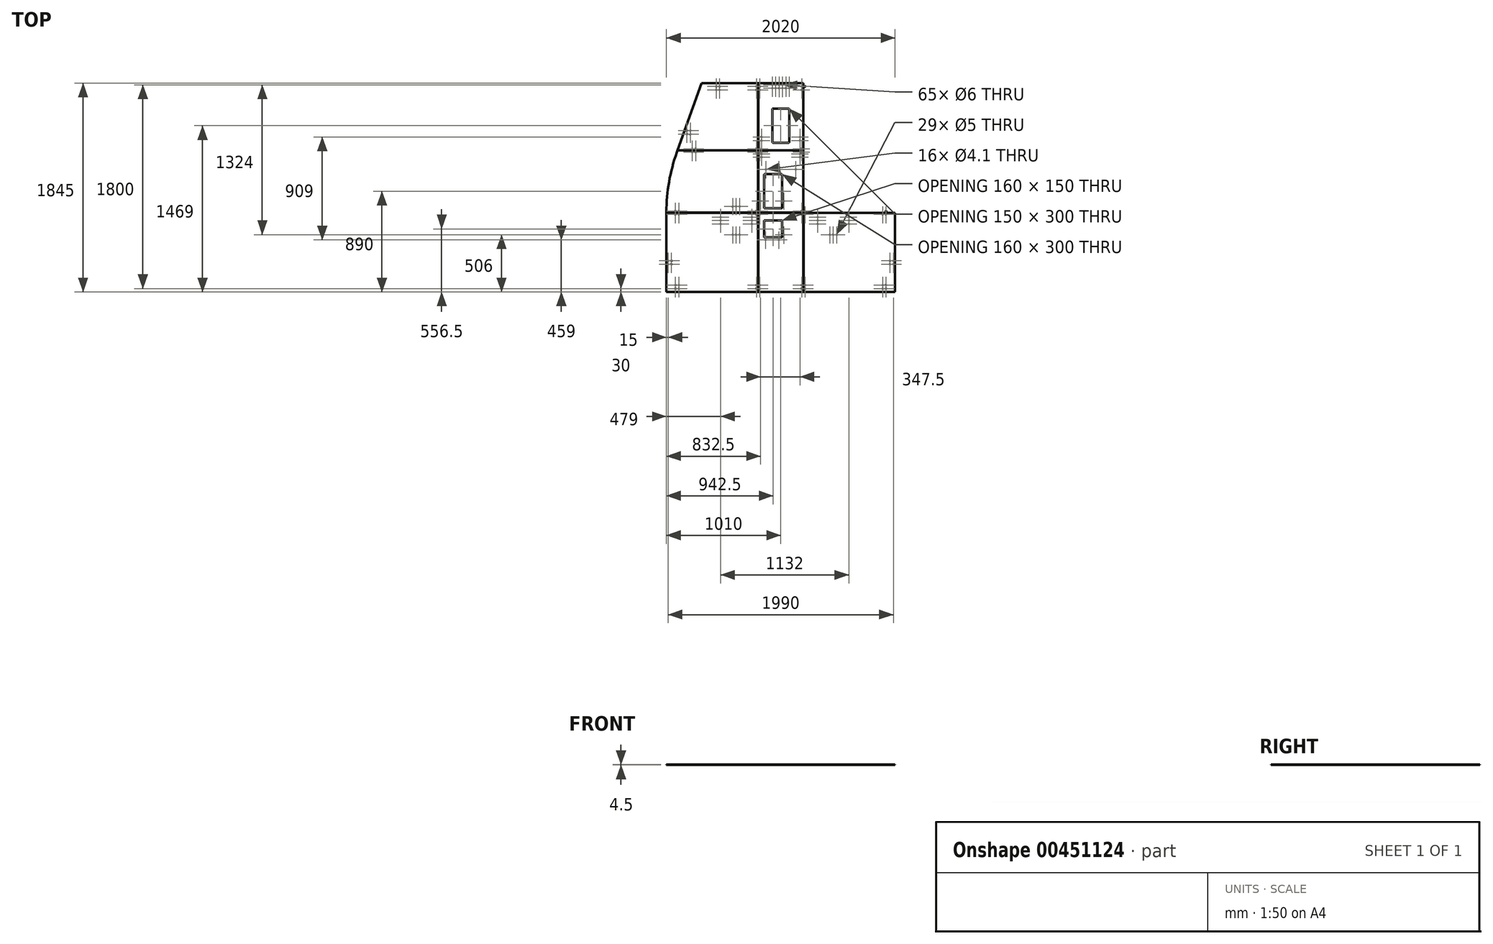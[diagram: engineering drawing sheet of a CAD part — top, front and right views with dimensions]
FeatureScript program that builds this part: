
annotation { "Feature Type Name" : "Feature", "Feature Type Description" : "" }
export const myFeature = defineFeature(function(context is Context, id is Id, definition is map)
    precondition{}
    {
        {
            var Q0;
            Q0=qCreatedBy(makeId("Top.planeOp"),FACE);
            var sketch = newSketch(context, id + "F0", { "sketchPlane" : qUnion([Q0])});
            skLineSegment(sketch, "E0.bottom", {"start": v(200, -350) * mm, "end": v(-200, -350) * mm});
            skLineSegment(sketch, "E0.top", {"start": v(200, 350) * mm, "end": v(-200, 350) * mm});
            skLineSegment(sketch, "E0.left", {"start": v(200, -350) * mm, "end": v(200, 350) * mm});
            skLineSegment(sketch, "E0.right", {"start": v(-200, -350) * mm, "end": v(-200, 350) * mm});
            skPoint(sketch, "E0.middle", {"position": v(0, 0) * mm});
            skCircle(sketch, "E1", {"center": v(185, 335) * mm, "radius": 3 * mm});
            skCircle(sketch, "E2", {"center": v(-185, 335) * mm, "radius": 3 * mm});
            skCircle(sketch, "E3", {"center": v(185, -320) * mm, "radius": 3 * mm});
            skCircle(sketch, "E4", {"center": v(-185, -320) * mm, "radius": 3 * mm});
            skLineSegment(sketch, "E5.bottom", {"start": v(12.5, 131.5) * mm, "end": v(-147.5, 131.5) * mm});
            skLineSegment(sketch, "E5.top", {"start": v(12.5, 281.5) * mm, "end": v(-147.5, 281.5) * mm});
            skLineSegment(sketch, "E5.left", {"start": v(12.5, 131.5) * mm, "end": v(12.5, 281.5) * mm});
            skLineSegment(sketch, "E5.right", {"start": v(-147.5, 131.5) * mm, "end": v(-147.5, 281.5) * mm});
            skPoint(sketch, "E5.middle", {"position": v(-67.5, 206.5) * mm});
            skCircle(sketch, "E6", {"center": v(-134.5, 109) * mm, "radius": 2.05 * mm});
            skCircle(sketch, "E7", {"center": v(-17.5, 109) * mm, "radius": 2.05 * mm});
            skCircle(sketch, "E8", {"center": v(27.5, 154) * mm, "radius": 2.05 * mm});
            skCircle(sketch, "E9", {"center": v(-185, -290) * mm, "radius": 3 * mm});
            skCircle(sketch, "E10", {"center": v(185, -290) * mm, "radius": 3 * mm});
            skSolve(sketch);
        }
        {
            var Q0;
            Q0=qSketchRegion(id+"F0",true);
            extrude(context, id + "F1", {"entities" : qUnion([Q0]), "depth" : 4.5 * mm, "offsetDistance" : 25 * mm});
        }
        {
            var Q0;
            Q0=qCreatedBy(makeId("Top.planeOp"),FACE);
            var sketch = newSketch(context, id + "F2", { "sketchPlane" : qUnion([Q0])});
            skLineSegment(sketch, "E11.top", {"start": v(-200, 900) * mm, "end": v(-912, 900) * mm});
            skLineSegment(sketch, "E11.left", {"start": v(-200, 350) * mm, "end": v(-200, 900) * mm});
            skPoint(sketch, "E11.middle", {"position": v(-556, 625) * mm});
            skLineSegment(sketch, "E12", {"start": v(-200, 350) * mm, "end": v(-1010, 350) * mm});
            skCircle(sketch, "E13", {"center": v(-215, 885) * mm, "radius": 3 * mm});
            skCircle(sketch, "E14", {"center": v(-215, 365) * mm, "radius": 3 * mm});
            skCircle(sketch, "E15", {"center": v(-930, 365) * mm, "radius": 3 * mm});
            skCircle(sketch, "E16", {"center": v(-782, 885) * mm, "radius": 3 * mm});
            skLineSegment(sketch, "E17.left", {"start": v(-200, 900) * mm, "end": v(-200, 1495) * mm});
            skPoint(sketch, "E17.middle", {"position": v(-556, 1197.5) * mm});
            skLineSegment(sketch, "E18", {"start": v(-200, 1495) * mm, "end": v(-700, 1495) * mm});
            skLineSegment(sketch, "E19", {"start": v(-912, 900) * mm, "end": v(-700, 1495) * mm});
            skCircle(sketch, "E20", {"center": v(-215, 1465) * mm, "radius": 3 * mm});
            skCircle(sketch, "E21", {"center": v(-215, 915) * mm, "radius": 3 * mm});
            skCircle(sketch, "E22", {"center": v(-782, 915) * mm, "radius": 3 * mm});
            skCircle(sketch, "E23", {"center": v(-570, 1465) * mm, "radius": 3 * mm});
            skLineSegment(sketch, "E24", {"start": v(0, 1490.85) * mm, "end": v(0, 501.43) * mm, "construction": true});
            skCircle(sketch, "E25.MirrorC", {"center": v(215, 1465) * mm, "radius": 3 * mm});
            skCircle(sketch, "E26.MirrorC", {"center": v(930, 365) * mm, "radius": 3 * mm});
            skCircle(sketch, "E27.MirrorC", {"center": v(782, 885) * mm, "radius": 3 * mm});
            skCircle(sketch, "E28.MirrorC", {"center": v(782, 915) * mm, "radius": 3 * mm});
            skCircle(sketch, "E29.MirrorC", {"center": v(570, 1465) * mm, "radius": 3 * mm});
            skCircle(sketch, "E30.MirrorC", {"center": v(215, 885) * mm, "radius": 3 * mm});
            skCircle(sketch, "E31.MirrorC", {"center": v(215, 365) * mm, "radius": 3 * mm});
            skCircle(sketch, "E32.MirrorC", {"center": v(215, 915) * mm, "radius": 3 * mm});
            skLineSegment(sketch, "E33.MirrorCS", {"start": v(200, 1495) * mm, "end": v(700, 1495) * mm});
            skLineSegment(sketch, "E34.MirrorCS", {"start": v(1010, 350) * mm, "end": v(912, 900) * mm, "construction": true});
            skLineSegment(sketch, "E35.MirrorCS", {"start": v(200, 900) * mm, "end": v(912, 900) * mm});
            skPoint(sketch, "E36.MirrorP", {"position": v(556, 1197.5) * mm});
            skLineSegment(sketch, "E37.MirrorCS", {"start": v(200, 350) * mm, "end": v(200, 900) * mm});
            skPoint(sketch, "E38.MirrorP", {"position": v(556, 625) * mm});
            skLineSegment(sketch, "E39.MirrorCS", {"start": v(200, 350) * mm, "end": v(1010, 350) * mm});
            skLineSegment(sketch, "E40.MirrorCS", {"start": v(912, 900) * mm, "end": v(700, 1495) * mm});
            skLineSegment(sketch, "E41.MirrorCS", {"start": v(200, 900) * mm, "end": v(200, 1495) * mm});
            skCircle(sketch, "E42", {"center": v(-900, 365) * mm, "radius": 3 * mm});
            skCircle(sketch, "E43", {"center": v(-752, 885) * mm, "radius": 3 * mm});
            skCircle(sketch, "E44", {"center": v(-752, 915) * mm, "radius": 3 * mm});
            skCircle(sketch, "E45", {"center": v(-570, 1435) * mm, "radius": 3 * mm});
            skCircle(sketch, "E46", {"center": v(-540, 1465) * mm, "radius": 3 * mm});
            skCircle(sketch, "E47", {"center": v(-540, 1435) * mm, "radius": 3 * mm});
            skCircle(sketch, "E48", {"center": v(-215, 1435) * mm, "radius": 3 * mm});
            skCircle(sketch, "E49.MirrorC", {"center": v(215, 1435) * mm, "radius": 3 * mm});
            skCircle(sketch, "E50.MirrorC", {"center": v(540, 1465) * mm, "radius": 3 * mm});
            skCircle(sketch, "E51.MirrorC", {"center": v(540, 1435) * mm, "radius": 3 * mm});
            skCircle(sketch, "E52.MirrorC", {"center": v(570, 1435) * mm, "radius": 3 * mm});
            skCircle(sketch, "E53.MirrorC", {"center": v(752, 915) * mm, "radius": 3 * mm});
            skCircle(sketch, "E54.MirrorC", {"center": v(752, 885) * mm, "radius": 3 * mm});
            skCircle(sketch, "E55.MirrorC", {"center": v(900, 365) * mm, "radius": 3 * mm});
            skCircle(sketch, "E56", {"center": v(-828.5, 1075) * mm, "radius": 3 * mm});
            skCircle(sketch, "E57", {"center": v(-798.5, 1075) * mm, "radius": 3 * mm});
            skCircle(sketch, "E58", {"center": v(-828.5, 1045) * mm, "radius": 3 * mm});
            skCircle(sketch, "E59", {"center": v(-798.5, 1045) * mm, "radius": 3 * mm});
            skCircle(sketch, "E60.MirrorC", {"center": v(828.5, 1045) * mm, "radius": 3 * mm});
            skCircle(sketch, "E61.MirrorC", {"center": v(798.5, 1075) * mm, "radius": 3 * mm});
            skCircle(sketch, "E62.MirrorC", {"center": v(828.5, 1075) * mm, "radius": 3 * mm});
            skCircle(sketch, "E63.MirrorC", {"center": v(798.5, 1045) * mm, "radius": 3 * mm});
            skCircle(sketch, "E64", {"center": v(-423.5, 406) * mm, "radius": 2.5 * mm});
            skCircle(sketch, "E65", {"center": v(-393.5, 406) * mm, "radius": 2.5 * mm});
            skCircle(sketch, "E66", {"center": v(-363.5, 406) * mm, "radius": 2.5 * mm});
            skCircle(sketch, "E67", {"center": v(433.5, 406) * mm, "radius": 2.5 * mm});
            skCircle(sketch, "E68", {"center": v(463.5, 406) * mm, "radius": 2.5 * mm});
            skCircle(sketch, "E69", {"center": v(493.5, 406) * mm, "radius": 2.5 * mm});
            skLineSegment(sketch, "E70", {"start": v(-912, 900) * mm, "end": v(-918.71, 881.16) * mm});
            skLineSegment(sketch, "E71", {"start": v(-1010, 350) * mm, "end": v(-1010, 370) * mm});
            skArc(sketch, "E72", {"start": v(-918.71, 881.16) * mm, "mid": v(-987.26, 619.52) * mm, "end": v(-1010, 350) * mm});
            skLineSegment(sketch, "E73.MirrorCS", {"start": v(912, 900) * mm, "end": v(918.71, 881.16) * mm});
            skArc(sketch, "E74.MirrorCS", {"start": v(918.71, 881.16) * mm, "mid": v(987.26, 619.52) * mm, "end": v(1010, 350) * mm});
            skSolve(sketch);
        }
        {
            var Q0;
            Q0=makeQuery(id+"F2.imprint","IMPRINT",FACE,{"disambiguationData":[TD([[makeQuery(id+"F2.imprint","IMPRINT",EDGE,{"derivedFrom":sQuery(id+"F2.wireOp",EDGE,"E11.left")}),1.0]])]});
            var Q1;
            Q1=makeQuery(id+"F2.imprint","IMPRINT",FACE,{"disambiguationData":[TD([[makeQuery(id+"F2.imprint","IMPRINT",EDGE,{"derivedFrom":sQuery(id+"F2.wireOp",EDGE,"E26.MirrorC")}),1.0]])]});
            extrude(context, id + "F3", {"entities" : qUnion([Q0, Q1]), "depth" : 4.5 * mm, "offsetDistance" : 25 * mm});
        }
        {
            var Q0;
            Q0=makeQuery(id+"F2.imprint","IMPRINT",FACE,{"disambiguationData":[TD([[makeQuery(id+"F2.imprint","IMPRINT",EDGE,{"derivedFrom":sQuery(id+"F2.wireOp",EDGE,"E11.top")}),-1.0]])]});
            var Q1;
            Q1=makeQuery(id+"F2.imprint","IMPRINT",FACE,{"disambiguationData":[TD([[makeQuery(id+"F2.imprint","IMPRINT",EDGE,{"derivedFrom":sQuery(id+"F2.wireOp",EDGE,"E25.MirrorC")}),1.0]])]});
            extrude(context, id + "F4", {"entities" : qUnion([Q0, Q1]), "depth" : 4.5 * mm, "offsetDistance" : 25 * mm});
        }
        {
            var Q0;
            Q0=qCreatedBy(makeId("Top.planeOp"),FACE);
            var sketch = newSketch(context, id + "F5", { "sketchPlane" : qUnion([Q0])});
            skLineSegment(sketch, "E75.bottom", {"start": v(200, 900) * mm, "end": v(-200, 900) * mm});
            skLineSegment(sketch, "E75.top", {"start": v(200, 350) * mm, "end": v(-200, 350) * mm});
            skLineSegment(sketch, "E75.left", {"start": v(200, 900) * mm, "end": v(200, 350) * mm});
            skLineSegment(sketch, "E75.right", {"start": v(-200, 900) * mm, "end": v(-200, 350) * mm});
            skPoint(sketch, "E75.middle", {"position": v(0, 625) * mm});
            skCircle(sketch, "E76", {"center": v(-132.5, 731.6) * mm, "radius": 2.05 * mm});
            skCircle(sketch, "E77", {"center": v(-17.5, 731.6) * mm, "radius": 2.05 * mm});
            skCircle(sketch, "E78", {"center": v(132.5, 731.6) * mm, "radius": 2.05 * mm});
            skCircle(sketch, "E79", {"center": v(-185, 885) * mm, "radius": 3 * mm});
            skCircle(sketch, "E80", {"center": v(185, 885) * mm, "radius": 3 * mm});
            skCircle(sketch, "E81", {"center": v(-185, 365) * mm, "radius": 3 * mm});
            skCircle(sketch, "E82", {"center": v(185, 365) * mm, "radius": 3 * mm});
            skCircle(sketch, "E83", {"center": v(170, 870) * mm, "radius": 2.05 * mm});
            skCircle(sketch, "E84", {"center": v(170, 840) * mm, "radius": 2.05 * mm});
            skLineSegment(sketch, "E85", {"start": v(0, 625) * mm, "end": v(0, 499.57) * mm, "construction": true});
            skCircle(sketch, "E86.MirrorC", {"center": v(-170, 840) * mm, "radius": 2.05 * mm});
            skCircle(sketch, "E87.MirrorC", {"center": v(-170, 870) * mm, "radius": 2.05 * mm});
            skLineSegment(sketch, "E88.bottom", {"start": v(12.5, 390) * mm, "end": v(-147.5, 390) * mm});
            skLineSegment(sketch, "E88.top", {"start": v(12.5, 690) * mm, "end": v(-147.5, 690) * mm});
            skLineSegment(sketch, "E88.left", {"start": v(12.5, 390) * mm, "end": v(12.5, 690) * mm});
            skLineSegment(sketch, "E88.right", {"start": v(-147.5, 390) * mm, "end": v(-147.5, 690) * mm});
            skPoint(sketch, "E88.middle", {"position": v(-67.5, 540) * mm});
            skCircle(sketch, "E89", {"center": v(-177.5, 454) * mm, "radius": 2.05 * mm});
            skCircle(sketch, "E90", {"center": v(27.5, 454) * mm, "radius": 2.05 * mm});
            skSolve(sketch);
        }
        {
            var Q0;
            Q0=qSketchRegion(id+"F5",true);
            extrude(context, id + "F6", {"entities" : qUnion([Q0]), "depth" : 4.5 * mm, "offsetDistance" : 25 * mm});
        }
        {
            var Q0;
            Q0=qCreatedBy(makeId("Top.planeOp"),FACE);
            var sketch = newSketch(context, id + "F7", { "sketchPlane" : qUnion([Q0])});
            skLineSegment(sketch, "E91.bottom", {"start": v(-200, 900) * mm, "end": v(200, 900) * mm});
            skLineSegment(sketch, "E91.top", {"start": v(200, 1495) * mm, "end": v(-200, 1495) * mm});
            skLineSegment(sketch, "E91.left", {"start": v(-200, 900) * mm, "end": v(-200, 1495) * mm});
            skLineSegment(sketch, "E91.right", {"start": v(200, 900) * mm, "end": v(200, 1495) * mm});
            skPoint(sketch, "E91.middle", {"position": v(0, 1197.5) * mm});
            skCircle(sketch, "E92", {"center": v(170, 970) * mm, "radius": 2.05 * mm, "construction": true});
            skCircle(sketch, "E93", {"center": v(170, 940) * mm, "radius": 2.05 * mm, "construction": true});
            skCircle(sketch, "E94", {"center": v(170, 988) * mm, "radius": 2.05 * mm});
            skCircle(sketch, "E95", {"center": v(170, 1018) * mm, "radius": 2.05 * mm});
            skCircle(sketch, "E96.MirrorC", {"center": v(-170, 970) * mm, "radius": 2.05 * mm, "construction": true});
            skCircle(sketch, "E97.MirrorC", {"center": v(-170, 988) * mm, "radius": 2.05 * mm});
            skCircle(sketch, "E98.MirrorC", {"center": v(-170, 1018) * mm, "radius": 2.05 * mm});
            skCircle(sketch, "E99.MirrorC", {"center": v(-170, 940) * mm, "radius": 2.05 * mm, "construction": true});
            skCircle(sketch, "E100", {"center": v(185, 1465) * mm, "radius": 3 * mm});
            skCircle(sketch, "E101", {"center": v(-185, 1465) * mm, "radius": 3 * mm});
            skCircle(sketch, "E102", {"center": v(185, 915) * mm, "radius": 3 * mm});
            skCircle(sketch, "E103", {"center": v(-185, 915) * mm, "radius": 3 * mm});
            skCircle(sketch, "E104", {"center": v(-185, 1435) * mm, "radius": 3 * mm});
            skCircle(sketch, "E105", {"center": v(185, 1435) * mm, "radius": 3 * mm});
            skLineSegment(sketch, "E106.bottom", {"start": v(75, 969) * mm, "end": v(-75, 969) * mm});
            skLineSegment(sketch, "E106.top", {"start": v(75, 1269) * mm, "end": v(-75, 1269) * mm});
            skLineSegment(sketch, "E106.left", {"start": v(75, 969) * mm, "end": v(75, 1269) * mm});
            skLineSegment(sketch, "E106.right", {"start": v(-75, 969) * mm, "end": v(-75, 1269) * mm});
            skPoint(sketch, "E106.middle", {"position": v(0, 1119) * mm});
            skCircle(sketch, "E107", {"center": v(-15, 1480) * mm, "radius": 3 * mm});
            skCircle(sketch, "E108", {"center": v(15, 1480) * mm, "radius": 3 * mm});
            skCircle(sketch, "E109", {"center": v(-15, 1450) * mm, "radius": 3 * mm});
            skCircle(sketch, "E110", {"center": v(15, 1450) * mm, "radius": 3 * mm});
            skCircle(sketch, "E111", {"center": v(-45, 1480) * mm, "radius": 2.5 * mm});
            skCircle(sketch, "E112", {"center": v(-45, 1450) * mm, "radius": 2.5 * mm});
            skCircle(sketch, "E113", {"center": v(45, 1480) * mm, "radius": 2.5 * mm});
            skCircle(sketch, "E114", {"center": v(45, 1450) * mm, "radius": 2.5 * mm});
            skLineSegment(sketch, "E115", {"start": v(-30, 1503.65) * mm, "end": v(-30, 1424.1) * mm, "construction": true});
            skLineSegment(sketch, "E116", {"start": v(30, 1503.65) * mm, "end": v(30, 1416.1) * mm, "construction": true});
            skCircle(sketch, "E117", {"center": v(-75, 1480) * mm, "radius": 2.5 * mm});
            skCircle(sketch, "E118", {"center": v(-75, 1450) * mm, "radius": 2.5 * mm});
            skLineSegment(sketch, "E119", {"start": v(0, 1346.91) * mm, "end": v(0, 1609.08) * mm, "construction": true});
            skPoint(sketch, "E119.endSnap0", {"position": v(0, 1495) * mm});
            skCircle(sketch, "E120.MirrorC", {"center": v(75, 1450) * mm, "radius": 2.5 * mm});
            skCircle(sketch, "E121.MirrorC", {"center": v(75, 1480) * mm, "radius": 2.5 * mm});
            skSolve(sketch);
        }
        {
            var Q0;
            Q0=qSketchRegion(id+"F7",true);
            extrude(context, id + "F8", {"entities" : qUnion([Q0]), "depth" : 4.5 * mm, "offsetDistance" : 25 * mm});
        }
        {
            var Q0;
            Q0=qCreatedBy(makeId("Top.planeOp"),FACE);
            var sketch = newSketch(context, id + "F9", { "sketchPlane" : qUnion([Q0])});
            skLineSegment(sketch, "E122.bottom", {"start": v(-200, -350) * mm, "end": v(-1010, -350) * mm});
            skLineSegment(sketch, "E122.top", {"start": v(-200, 350) * mm, "end": v(-1010, 350) * mm});
            skLineSegment(sketch, "E122.left", {"start": v(-200, -350) * mm, "end": v(-200, 350) * mm});
            skLineSegment(sketch, "E122.right", {"start": v(-1010, -350) * mm, "end": v(-1010, 350) * mm});
            skPoint(sketch, "E122.middle", {"position": v(-605, 0) * mm});
            skPoint(sketch, "E123", {"position": v(-930, 335) * mm});
            skPoint(sketch, "E124", {"position": v(-215, 335) * mm});
            skPoint(sketch, "E125", {"position": v(-930, -320) * mm});
            skPoint(sketch, "E126", {"position": v(-215, -320) * mm});
            skCircle(sketch, "E127", {"center": v(-930, 335) * mm, "radius": 3 * mm});
            skCircle(sketch, "E128", {"center": v(-215, 335) * mm, "radius": 3 * mm});
            skCircle(sketch, "E129", {"center": v(-930, -320) * mm, "radius": 3 * mm});
            skCircle(sketch, "E130", {"center": v(-215, -320) * mm, "radius": 3 * mm});
            skLineSegment(sketch, "E131.bottom", {"start": v(200, -350) * mm, "end": v(1010, -350) * mm});
            skLineSegment(sketch, "E131.top", {"start": v(200, 350) * mm, "end": v(1010, 350) * mm});
            skLineSegment(sketch, "E131.left", {"start": v(200, -350) * mm, "end": v(200, 350) * mm});
            skLineSegment(sketch, "E131.right", {"start": v(1010, -350) * mm, "end": v(1010, 350) * mm});
            skPoint(sketch, "E131.middle", {"position": v(605, 0) * mm});
            skCircle(sketch, "E132", {"center": v(215, 335) * mm, "radius": 3 * mm});
            skCircle(sketch, "E133", {"center": v(930, 335) * mm, "radius": 3 * mm});
            skCircle(sketch, "E134", {"center": v(215, -320) * mm, "radius": 3 * mm});
            skCircle(sketch, "E135", {"center": v(930, -320) * mm, "radius": 3 * mm});
            skCircle(sketch, "E136", {"center": v(-930, -290) * mm, "radius": 3 * mm});
            skCircle(sketch, "E137", {"center": v(-900, -320) * mm, "radius": 3 * mm});
            skCircle(sketch, "E138", {"center": v(-900, -290) * mm, "radius": 3 * mm});
            skCircle(sketch, "E139", {"center": v(-215, -290) * mm, "radius": 3 * mm});
            skCircle(sketch, "E140", {"center": v(-900, 335) * mm, "radius": 3 * mm});
            skCircle(sketch, "E141", {"center": v(900, -320) * mm, "radius": 3 * mm});
            skCircle(sketch, "E142", {"center": v(930, -290) * mm, "radius": 3 * mm});
            skCircle(sketch, "E143", {"center": v(900, -290) * mm, "radius": 3 * mm});
            skCircle(sketch, "E144", {"center": v(215, -290) * mm, "radius": 3 * mm});
            skCircle(sketch, "E145", {"center": v(900, 335) * mm, "radius": 3 * mm});
            skCircle(sketch, "E146", {"center": v(-995, -75) * mm, "radius": 3 * mm});
            skCircle(sketch, "E147", {"center": v(-965, -75) * mm, "radius": 3 * mm});
            skCircle(sketch, "E148", {"center": v(-995, -105) * mm, "radius": 3 * mm});
            skCircle(sketch, "E149", {"center": v(-965, -105) * mm, "radius": 3 * mm});
            skCircle(sketch, "E150", {"center": v(995, -75) * mm, "radius": 3 * mm});
            skCircle(sketch, "E151", {"center": v(965, -75) * mm, "radius": 3 * mm});
            skCircle(sketch, "E152", {"center": v(965, -105) * mm, "radius": 3 * mm});
            skCircle(sketch, "E153", {"center": v(995, -105) * mm, "radius": 3 * mm});
            skCircle(sketch, "E154", {"center": v(601, 311) * mm, "radius": 2.5 * mm});
            skCircle(sketch, "E155", {"center": v(601, 281) * mm, "radius": 2.5 * mm});
            skCircle(sketch, "E156", {"center": v(601, 251) * mm, "radius": 2.5 * mm});
            skCircle(sketch, "E157", {"center": v(326, 311) * mm, "radius": 2.5 * mm});
            skCircle(sketch, "E158", {"center": v(326, 281) * mm, "radius": 2.5 * mm});
            skCircle(sketch, "E159", {"center": v(326, 251) * mm, "radius": 2.5 * mm});
            skLineSegment(sketch, "E160", {"start": v(0, -608.3) * mm, "end": v(0, 1601.34) * mm, "construction": true});
            skCircle(sketch, "E161", {"center": v(-256, 311) * mm, "radius": 2.5 * mm});
            skCircle(sketch, "E162", {"center": v(-256, 281) * mm, "radius": 2.5 * mm});
            skCircle(sketch, "E163", {"center": v(-256, 251) * mm, "radius": 2.5 * mm});
            skCircle(sketch, "E164", {"center": v(-531, 311) * mm, "radius": 2.5 * mm});
            skCircle(sketch, "E165", {"center": v(-531, 281) * mm, "radius": 2.5 * mm});
            skCircle(sketch, "E166", {"center": v(-531, 251) * mm, "radius": 2.5 * mm});
            skCircle(sketch, "E167", {"center": v(433.5, 156) * mm, "radius": 2.5 * mm});
            skCircle(sketch, "E168", {"center": v(463.5, 156) * mm, "radius": 2.5 * mm});
            skCircle(sketch, "E169", {"center": v(493.5, 156) * mm, "radius": 2.5 * mm});
            skCircle(sketch, "E170", {"center": v(-423.5, 156) * mm, "radius": 2.5 * mm});
            skCircle(sketch, "E171", {"center": v(-393.5, 156) * mm, "radius": 2.5 * mm});
            skCircle(sketch, "E172", {"center": v(-363.5, 156) * mm, "radius": 2.5 * mm});
            skSolve(sketch);
        }
        {
            var Q0;
            Q0=qSketchRegion(id+"F9",true);
            extrude(context, id + "F10", {"entities" : qUnion([Q0]), "depth" : 4.5 * mm, "offsetDistance" : 25 * mm});
        }
        {
            var Q0;
            Q0=qCreatedBy(makeId("Top.planeOp"),FACE);
            cPlane(context, id + "F11", {"entities" : qUnion([Q0]), "cplaneType" : CPlaneType.OFFSET, "offset" : 8.5 * mm, "width" : 150 * mm, "height" : 150 * mm});
        }
        {
            var Q0;
            Q0=qCreatedBy(id+"F11.planeOp",FACE);
            var sketch = newSketch(context, id + "F12", { "sketchPlane" : qUnion([Q0])});
            skLineSegment(sketch, "E173.bottom", {"start": v(-1260.85, 350.5) * mm, "end": v(1232.58, 350.5) * mm});
            skLineSegment(sketch, "E173.top", {"start": v(-1260.85, 349.5) * mm, "end": v(1232.58, 349.5) * mm});
            skLineSegment(sketch, "E173.left", {"start": v(-1260.85, 350.5) * mm, "end": v(-1260.85, 349.5) * mm});
            skLineSegment(sketch, "E173.right", {"start": v(1232.58, 350.5) * mm, "end": v(1232.58, 349.5) * mm});
            skLineSegment(sketch, "E174.bottom", {"start": v(-1136.47, 900.5) * mm, "end": v(1063.53, 900.5) * mm});
            skLineSegment(sketch, "E174.top", {"start": v(-1136.47, 899.5) * mm, "end": v(1063.53, 899.5) * mm});
            skLineSegment(sketch, "E174.left", {"start": v(-1136.47, 900.5) * mm, "end": v(-1136.47, 899.5) * mm});
            skLineSegment(sketch, "E174.right", {"start": v(1063.53, 900.5) * mm, "end": v(1063.53, 899.5) * mm});
            skLineSegment(sketch, "E175.bottom", {"start": v(-200.5, 1591.24) * mm, "end": v(-199.5, 1591.24) * mm});
            skLineSegment(sketch, "E175.top", {"start": v(-200.5, -431.72) * mm, "end": v(-199.5, -431.72) * mm});
            skLineSegment(sketch, "E175.left", {"start": v(-200.5, 1591.24) * mm, "end": v(-200.5, -431.72) * mm});
            skLineSegment(sketch, "E175.right", {"start": v(-199.5, 1591.24) * mm, "end": v(-199.5, -431.72) * mm});
            skLineSegment(sketch, "E176.bottom", {"start": v(199.5, 1591.24) * mm, "end": v(200.5, 1591.24) * mm});
            skLineSegment(sketch, "E176.top", {"start": v(199.5, -431.72) * mm, "end": v(200.5, -431.72) * mm});
            skLineSegment(sketch, "E176.left", {"start": v(199.5, 1591.24) * mm, "end": v(199.5, -431.72) * mm});
            skLineSegment(sketch, "E176.right", {"start": v(200.5, 1591.24) * mm, "end": v(200.5, -431.72) * mm});
            skSolve(sketch);
        }
        {
            var Q0;
            Q0=qSketchRegion(id+"F12",true);
            extrude(context, id + "F13", {"entities" : qUnion([Q0]), "operationType" : NewBodyOperationType.REMOVE, "oppositeDirection" : true, "depth" : 25 * mm, "offsetDistance" : 25 * mm});
        }
        {
            var Q0;
            Q0=makeQuery(id+"F1.opExtrude","SWEPT_EDGE",EDGE,{"disambiguationData":[OSD([sQuery(id+"F0.wireOp",EDGE,"E5.bottom"),sQuery(id+"F0.wireOp",EDGE,"E5.right")])]});
            var Q1;
            Q1=makeQuery(id+"F1.opExtrude","SWEPT_EDGE",EDGE,{"disambiguationData":[OSD([sQuery(id+"F0.wireOp",EDGE,"E5.bottom"),sQuery(id+"F0.wireOp",EDGE,"E5.left")])]});
            var Q2;
            Q2=makeQuery(id+"F1.opExtrude","SWEPT_EDGE",EDGE,{"disambiguationData":[OSD([sQuery(id+"F0.wireOp",EDGE,"E5.top"),sQuery(id+"F0.wireOp",EDGE,"E5.left")])]});
            var Q3;
            Q3=makeQuery(id+"F1.opExtrude","SWEPT_EDGE",EDGE,{"disambiguationData":[OSD([sQuery(id+"F0.wireOp",EDGE,"E5.top"),sQuery(id+"F0.wireOp",EDGE,"E5.right")])]});
            var Q4;
            Q4=makeQuery(id+"F6.opExtrude","SWEPT_EDGE",EDGE,{"disambiguationData":[OSD([sQuery(id+"F5.wireOp",EDGE,"E88.bottom"),sQuery(id+"F5.wireOp",EDGE,"E88.right")])]});
            var Q5;
            Q5=makeQuery(id+"F6.opExtrude","SWEPT_EDGE",EDGE,{"disambiguationData":[OSD([sQuery(id+"F5.wireOp",EDGE,"E88.bottom"),sQuery(id+"F5.wireOp",EDGE,"E88.left")])]});
            var Q6;
            Q6=makeQuery(id+"F6.opExtrude","SWEPT_EDGE",EDGE,{"disambiguationData":[OSD([sQuery(id+"F5.wireOp",EDGE,"E88.top"),sQuery(id+"F5.wireOp",EDGE,"E88.right")])]});
            var Q7;
            Q7=makeQuery(id+"F6.opExtrude","SWEPT_EDGE",EDGE,{"disambiguationData":[OSD([sQuery(id+"F5.wireOp",EDGE,"E88.top"),sQuery(id+"F5.wireOp",EDGE,"E88.left")])]});
            var Q8;
            Q8=makeQuery(id+"F8.opExtrude","SWEPT_EDGE",EDGE,{"disambiguationData":[OSD([sQuery(id+"F7.wireOp",EDGE,"E106.top"),sQuery(id+"F7.wireOp",EDGE,"E106.left")])]});
            var Q9;
            Q9=makeQuery(id+"F8.opExtrude","SWEPT_EDGE",EDGE,{"disambiguationData":[OSD([sQuery(id+"F7.wireOp",EDGE,"E106.top"),sQuery(id+"F7.wireOp",EDGE,"E106.right")])]});
            var Q10;
            Q10=makeQuery(id+"F8.opExtrude","SWEPT_EDGE",EDGE,{"disambiguationData":[OSD([sQuery(id+"F7.wireOp",EDGE,"E106.bottom"),sQuery(id+"F7.wireOp",EDGE,"E106.right")])]});
            var Q11;
            Q11=makeQuery(id+"F8.opExtrude","SWEPT_EDGE",EDGE,{"disambiguationData":[OSD([sQuery(id+"F7.wireOp",EDGE,"E106.bottom"),sQuery(id+"F7.wireOp",EDGE,"E106.left")])]});
            fillet(context, id + "F14", {"entities" : qUnion([Q0, Q1, Q2, Q3, Q4, Q5, Q6, Q7, Q8, Q9, Q10, Q11]), "radius" : 5 * mm, "tangentPropagation" : true, "allowEdgeOverflow" : false});
        }
    });
